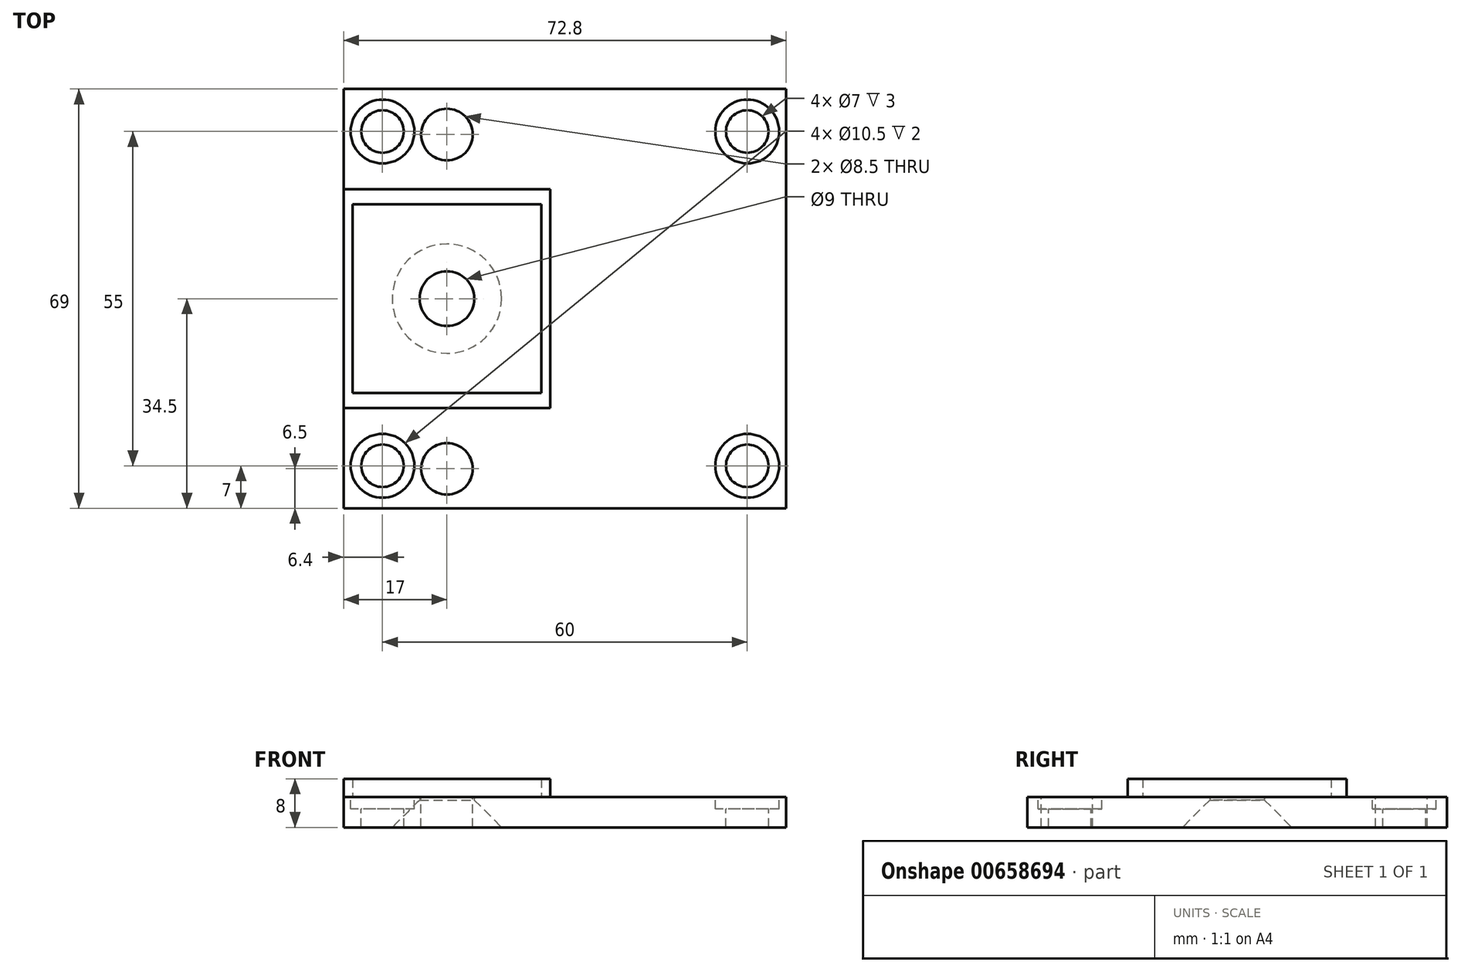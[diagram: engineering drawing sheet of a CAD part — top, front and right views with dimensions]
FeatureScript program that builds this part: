
annotation { "Feature Type Name" : "Feature", "Feature Type Description" : "" }
export const myFeature = defineFeature(function(context is Context, id is Id, definition is map)
    precondition{}
    {
        {
            var Q0;
            Q0=qCreatedBy(makeId("Top.planeOp"),FACE);
            var sketch = newSketch(context, id + "F0", { "sketchPlane" : qUnion([Q0])});
            skLineSegment(sketch, "E0.rect.bottom", {"start": v(36.4, -34.5) * mm, "end": v(-36.4, -34.5) * mm});
            skLineSegment(sketch, "E0.rect.top", {"start": v(36.4, 34.5) * mm, "end": v(-36.4, 34.5) * mm});
            skLineSegment(sketch, "E0.rect.left", {"start": v(36.4, -34.5) * mm, "end": v(36.4, 34.5) * mm});
            skLineSegment(sketch, "E0.rect.right", {"start": v(-36.4, -34.5) * mm, "end": v(-36.4, 34.5) * mm});
            skPoint(sketch, "E0.rect.middle", {"position": v(0, 0) * mm});
            skSolve(sketch);
        }
        {
            var Q0;
            Q0=makeQuery(id+"F0.imprint","IMPRINT",FACE,{"disambiguationData":[TD([[makeQuery(id+"F0.imprint","IMPRINT",EDGE,{"derivedFrom":sQuery(id+"F0.wireOp",EDGE,"E0.rect.bottom")}),-1.0]])]});
            extrude(context, id + "F1", {"entities" : qUnion([Q0]), "depth" : 5 * mm});
        }
        {
            var Q0;
            Q0=makeQuery(id+"F1.opExtrude","CAP_FACE",FACE,{"disambiguationData":[OSD([sQuery(id+"F0.wireOp",EDGE,"E0.rect.bottom"),sQuery(id+"F0.wireOp",EDGE,"E0.rect.top"),sQuery(id+"F0.wireOp",EDGE,"E0.rect.left"),sQuery(id+"F0.wireOp",EDGE,"E0.rect.right")])],"isStart":false});
            var sketch = newSketch(context, id + "F2", { "sketchPlane" : qUnion([Q0])});
            skPoint(sketch, "E1", {"position": v(-30, 27.5) * mm});
            skPoint(sketch, "E2", {"position": v(30, 27.5) * mm});
            skPoint(sketch, "E3", {"position": v(30, -27.5) * mm});
            skPoint(sketch, "E4", {"position": v(-30, -27.5) * mm});
            skLineSegment(sketch, "E5.0", {"start": v(36.4, 34.5) * mm, "end": v(-36.4, 34.5) * mm});
            skLineSegment(sketch, "E6.0", {"start": v(36.4, -34.5) * mm, "end": v(-36.4, -34.5) * mm});
            skSolve(sketch);
        }
        {
            var Q0;
            Q0=sQuery(id+"F2.wireOp",VERTEX,"E1");
            var Q1;
            Q1=sQuery(id+"F2.wireOp",VERTEX,"E2");
            var Q2;
            Q2=sQuery(id+"F2.wireOp",VERTEX,"E3");
            var Q3;
            Q3=sQuery(id+"F2.wireOp",VERTEX,"E4");
            var Q4;
            Q4=makeQuery(id+"F1.opExtrude","SWEPT_BODY",BODY,{"disambiguationData":[OSD([sQuery(id+"F0.wireOp",EDGE,"E0.rect.bottom"),sQuery(id+"F0.wireOp",EDGE,"E0.rect.top"),sQuery(id+"F0.wireOp",EDGE,"E0.rect.left"),sQuery(id+"F0.wireOp",EDGE,"E0.rect.right")])]});
            hole(context, id + "F3", {"style" : HoleStyle.SIMPLE, "holeDiameter" : 7 * mm, "endStyle" : HoleEndStyle.THROUGH, "locations" : qUnion([Q0, Q1, Q2, Q3]), "scope" : qUnion([Q4])});
        }
        {
            var Q0;
            Q0=makeQuery(id+"F1.opExtrude","CAP_FACE",FACE,{"disambiguationData":[OSD([sQuery(id+"F0.wireOp",EDGE,"E0.rect.bottom"),sQuery(id+"F0.wireOp",EDGE,"E0.rect.top"),sQuery(id+"F0.wireOp",EDGE,"E0.rect.left"),sQuery(id+"F0.wireOp",EDGE,"E0.rect.right")])],"isStart":false});
            var sketch = newSketch(context, id + "F4", { "sketchPlane" : qUnion([Q0])});
            skPoint(sketch, "E7", {"position": v(-19.4, 27) * mm});
            skPoint(sketch, "E8", {"position": v(-19.4, -28) * mm});
            skSolve(sketch);
        }
        {
            var Q0;
            Q0=sQuery(id+"F4.wireOp",VERTEX,"E7");
            var Q1;
            Q1=sQuery(id+"F4.wireOp",VERTEX,"E8");
            var Q2;
            Q2=makeQuery(id+"F1.opExtrude","SWEPT_BODY",BODY,{"disambiguationData":[OSD([sQuery(id+"F0.wireOp",EDGE,"E0.rect.bottom"),sQuery(id+"F0.wireOp",EDGE,"E0.rect.top"),sQuery(id+"F0.wireOp",EDGE,"E0.rect.left"),sQuery(id+"F0.wireOp",EDGE,"E0.rect.right")])]});
            hole(context, id + "F5", {"style" : HoleStyle.SIMPLE, "holeDiameter" : 8.5 * mm, "endStyle" : HoleEndStyle.THROUGH, "locations" : qUnion([Q0, Q1]), "scope" : qUnion([Q2])});
        }
        {
            var Q0;
            Q0=makeQuery(id+"F1.opExtrude","CAP_FACE",FACE,{"disambiguationData":[OSD([sQuery(id+"F0.wireOp",EDGE,"E0.rect.bottom"),sQuery(id+"F0.wireOp",EDGE,"E0.rect.top"),sQuery(id+"F0.wireOp",EDGE,"E0.rect.left"),sQuery(id+"F0.wireOp",EDGE,"E0.rect.right")])],"isStart":false});
            var sketch = newSketch(context, id + "F6", { "sketchPlane" : qUnion([Q0])});
            skLineSegment(sketch, "E9.rect.bottom", {"start": v(-3.9, 15.5) * mm, "end": v(-34.9, 15.5) * mm});
            skLineSegment(sketch, "E9.rect.top", {"start": v(-3.9, -15.5) * mm, "end": v(-34.9, -15.5) * mm});
            skLineSegment(sketch, "E9.rect.left", {"start": v(-3.9, 15.5) * mm, "end": v(-3.9, -15.5) * mm});
            skLineSegment(sketch, "E9.rect.right", {"start": v(-34.9, 15.5) * mm, "end": v(-34.9, -15.5) * mm});
            skPoint(sketch, "E9.rect.middle", {"position": v(-19.4, 0) * mm});
            skLineSegment(sketch, "E10.rect.bottom", {"start": v(-36.4, 18) * mm, "end": v(-2.4, 18) * mm});
            skLineSegment(sketch, "E10.rect.top", {"start": v(-36.4, -18) * mm, "end": v(-2.4, -18) * mm});
            skLineSegment(sketch, "E10.rect.left", {"start": v(-36.4, 18) * mm, "end": v(-36.4, -18) * mm});
            skLineSegment(sketch, "E10.rect.right", {"start": v(-2.4, 18) * mm, "end": v(-2.4, -18) * mm});
            skSolve(sketch);
        }
        {
            var Q0;
            Q0=makeQuery(id+"F6.imprint","IMPRINT",FACE,{"disambiguationData":[TD([[makeQuery(id+"F6.imprint","IMPRINT",EDGE,{"derivedFrom":sQuery(id+"F6.wireOp",EDGE,"E9.rect.bottom")}),-1.0]])]});
            extrude(context, id + "F7", {"entities" : qUnion([Q0]), "operationType" : NewBodyOperationType.ADD, "depth" : 3 * mm});
        }
        {
            var Q0;
            Q0=makeQuery(id+"F1.opExtrude","CAP_FACE",FACE,{"disambiguationData":[OSD([sQuery(id+"F0.wireOp",EDGE,"E0.rect.bottom"),sQuery(id+"F0.wireOp",EDGE,"E0.rect.top"),sQuery(id+"F0.wireOp",EDGE,"E0.rect.left"),sQuery(id+"F0.wireOp",EDGE,"E0.rect.right")])],"isStart":true});
            var sketch = newSketch(context, id + "F8", { "sketchPlane" : qUnion([Q0])});
            skLineSegment(sketch, "E11.0.0", {"start": v(-3.9, 15.5) * mm, "end": v(-3.9, -15.5) * mm});
            skLineSegment(sketch, "E11.0.1", {"start": v(-3.9, -15.5) * mm, "end": v(-34.9, -15.5) * mm});
            skLineSegment(sketch, "E11.0.2", {"start": v(-34.9, -15.5) * mm, "end": v(-34.9, 15.5) * mm});
            skLineSegment(sketch, "E11.0.3", {"start": v(-34.9, 15.5) * mm, "end": v(-3.9, 15.5) * mm});
            skLineSegment(sketch, "E12", {"start": v(-19.4, -15.5) * mm, "end": v(-19.4, 15.5) * mm, "construction": true});
            skPoint(sketch, "E13", {"position": v(-19.4, 0) * mm});
            skSolve(sketch);
        }
        {
            var Q0;
            Q0=sQuery(id+"F8.wireOp",VERTEX,"E13");
            var Q1;
            Q1=makeQuery(id+"F1.opExtrude","SWEPT_BODY",BODY,{"disambiguationData":[OSD([sQuery(id+"F0.wireOp",EDGE,"E0.rect.bottom"),sQuery(id+"F0.wireOp",EDGE,"E0.rect.top"),sQuery(id+"F0.wireOp",EDGE,"E0.rect.left"),sQuery(id+"F0.wireOp",EDGE,"E0.rect.right")])]});
            hole(context, id + "F9", {"style" : HoleStyle.C_SINK, "holeDiameter" : 9 * mm, "cSinkDiameter" : 18 * mm, "endStyle" : HoleEndStyle.THROUGH, "locations" : qUnion([Q0]), "scope" : qUnion([Q1]), "cSinkAngle" : 90 * degree});
        }
        {
            var Q0;
            {var subQ0=sQuery(id+"F0.wireOp",EDGE,"E0.rect.left");var subQ1=sQuery(id+"F0.wireOp",EDGE,"E0.rect.bottom");var subQ2=sQuery(id+"F0.wireOp",EDGE,"E0.rect.top");var subQ3=sQuery(id+"F0.wireOp",EDGE,"E0.rect.right");Q0=makeQuery(id+"F7.boolean.opBoolean","SPLIT",FACE,{"disambiguationData":[TD([makeQuery(id+"F1.opExtrude","SWEPT_FACE",FACE,{"disambiguationData":[OSD([subQ1])]})])],"derivedFrom":makeQuery(id+"F1.opExtrude","CAP_FACE",FACE,{"disambiguationData":[OSD([subQ1,subQ2,subQ0,subQ3])],"isStart":false})});}
            var sketch = newSketch(context, id + "F10", { "sketchPlane" : qUnion([Q0])});
            skCircle(sketch, "E14.0", {"center": v(-30, 27.5) * mm, "radius": 3.5 * mm});
            skCircle(sketch, "E15.0", {"center": v(30, 27.5) * mm, "radius": 3.5 * mm});
            skCircle(sketch, "E16.0", {"center": v(30, -27.5) * mm, "radius": 3.5 * mm});
            skCircle(sketch, "E17.0", {"center": v(-30, -27.5) * mm, "radius": 3.5 * mm});
            skSolve(sketch);
        }
        {
            var Q0;
            Q0=sQuery(id+"F10.wireOp",VERTEX,"E14.0.center");
            var Q1;
            Q1=sQuery(id+"F10.wireOp",VERTEX,"E15.0.center");
            var Q2;
            Q2=sQuery(id+"F10.wireOp",VERTEX,"E16.0.center");
            var Q3;
            Q3=sQuery(id+"F10.wireOp",VERTEX,"E17.0.center");
            var Q4;
            Q4=makeQuery(id+"F1.opExtrude","SWEPT_BODY",BODY,{"disambiguationData":[OSD([sQuery(id+"F0.wireOp",EDGE,"E0.rect.bottom"),sQuery(id+"F0.wireOp",EDGE,"E0.rect.top"),sQuery(id+"F0.wireOp",EDGE,"E0.rect.left"),sQuery(id+"F0.wireOp",EDGE,"E0.rect.right")])]});
            hole(context, id + "F11", {"style" : HoleStyle.C_BORE, "holeDiameter" : 7 * mm, "cBoreDiameter" : 10.5 * mm, "cBoreDepth" : 2 * mm, "endStyle" : HoleEndStyle.THROUGH, "locations" : qUnion([Q0, Q1, Q2, Q3]), "scope" : qUnion([Q4])});
        }
    });
